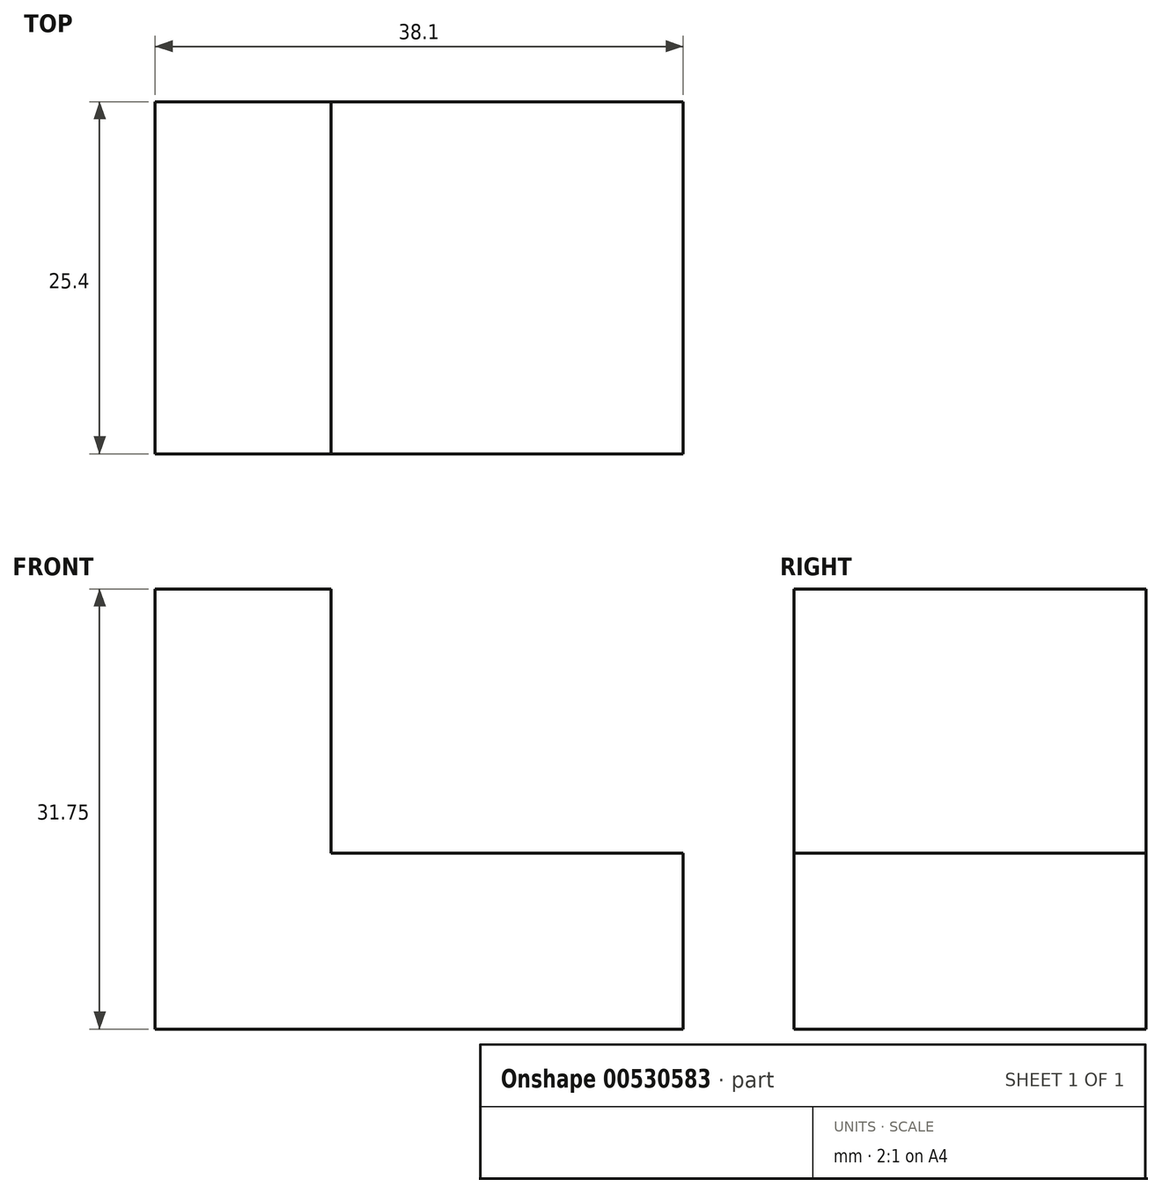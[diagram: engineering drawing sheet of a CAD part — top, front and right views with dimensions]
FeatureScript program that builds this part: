
annotation { "Feature Type Name" : "Feature", "Feature Type Description" : "" }
export const myFeature = defineFeature(function(context is Context, id is Id, definition is map)
    precondition{}
    {
        {
            var Q0;
            Q0=qCreatedBy(makeId("Front.planeOp"),FACE);
            var sketch = newSketch(context, id + "F0", { "sketchPlane" : qUnion([Q0])});
            skLineSegment(sketch, "E0", {"start": v(-68.86, 0) * mm, "end": v(-68.86, 31.75) * mm});
            skLineSegment(sketch, "E1", {"start": v(-68.86, 31.75) * mm, "end": v(-56.16, 31.75) * mm});
            skLineSegment(sketch, "E2", {"start": v(-56.16, 31.75) * mm, "end": v(-56.16, 12.7) * mm});
            skLineSegment(sketch, "E3", {"start": v(-56.16, 12.7) * mm, "end": v(-30.76, 12.7) * mm});
            skLineSegment(sketch, "E4", {"start": v(-30.76, 12.7) * mm, "end": v(-30.76, 0) * mm});
            skLineSegment(sketch, "E5", {"start": v(-30.76, 0) * mm, "end": v(-68.86, 0) * mm});
            skSolve(sketch);
        }
        {
            var Q0;
            Q0=makeQuery(id+"F0.imprint","IMPRINT",FACE,{"disambiguationData":[TD([[makeQuery(id+"F0.imprint","IMPRINT",EDGE,{"derivedFrom":sQuery(id+"F0.wireOp",EDGE,"E0")}),-1.0]])]});
            extrude(context, id + "F1", {"entities" : qUnion([Q0]), "depth" : 25.4 * mm, "offsetDistance" : 25.4 * mm});
        }
    });
